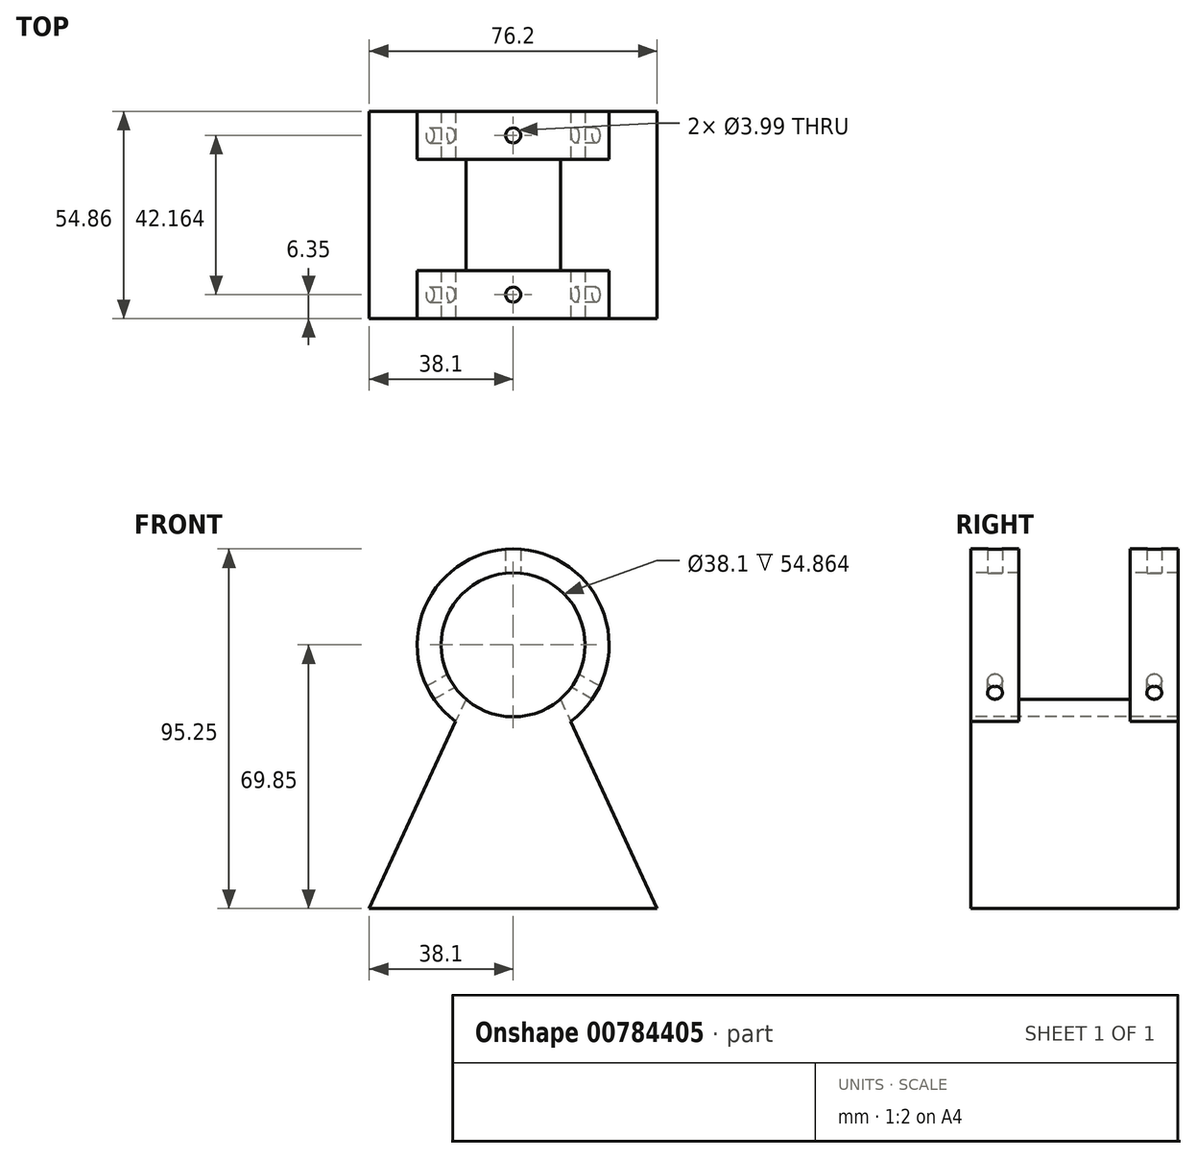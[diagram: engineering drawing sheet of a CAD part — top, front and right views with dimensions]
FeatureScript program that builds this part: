
annotation { "Feature Type Name" : "Feature", "Feature Type Description" : "" }
export const myFeature = defineFeature(function(context is Context, id is Id, definition is map)
    precondition{}
    {
        {
            var Q0;
            Q0=qCreatedBy(makeId("Front.planeOp"),FACE);
            var sketch = newSketch(context, id + "F0", { "sketchPlane" : qUnion([Q0])});
            skCircle(sketch, "E0", {"center": v(0, 69.85) * mm, "radius": 19.05 * mm});
            skArc(sketch, "E1", {"start": v(15.24, 49.53) * mm, "mid": v(0, 95.25) * mm, "end": v(-15.24, 49.53) * mm});
            skLineSegment(sketch, "E2", {"start": v(0, 44.45) * mm, "end": v(0, 49.53) * mm, "construction": true});
            skLineSegment(sketch, "E3", {"start": v(0, 49.53) * mm, "end": v(-15.24, 49.53) * mm, "construction": true});
            skLineSegment(sketch, "E4", {"start": v(-15.24, 49.53) * mm, "end": v(-38.1, 0) * mm});
            skLineSegment(sketch, "E5", {"start": v(-38.1, 0) * mm, "end": v(38.1, 0) * mm});
            skLineSegment(sketch, "E6", {"start": v(38.1, 0) * mm, "end": v(15.24, 49.53) * mm});
            skSolve(sketch);
        }
        {
            var Q0;
            Q0 = qSketchRegion(id + "F0", true);
            extrude(context, id + "F1", {"entities" : qUnion([Q0]), "oppositeDirection" : true, "depth" : 54.86 * mm, "offsetDistance" : 25.4 * mm});
        }
        {
            var Q0;
            Q0=qCreatedBy(makeId("Top.planeOp"),FACE);
            cPlane(context, id + "F2", {"entities" : qUnion([Q0]), "cplaneType" : CPlaneType.OFFSET, "offset" : 12.7 * mm, "width" : 152.4 * mm, "height" : 152.4 * mm});
        }
        {
            var Q0;
            Q0=qCreatedBy(id+"F2.planeOp",FACE);
            var sketch = newSketch(context, id + "F3", { "sketchPlane" : qUnion([Q0])});
            skLineSegment(sketch, "E7.bottom", {"start": v(-38.1, 12.7) * mm, "end": v(38.1, 12.7) * mm});
            skLineSegment(sketch, "E7.top", {"start": v(-38.1, 42.16) * mm, "end": v(38.1, 42.16) * mm});
            skLineSegment(sketch, "E7.left", {"start": v(-38.1, 12.7) * mm, "end": v(-38.1, 42.16) * mm});
            skLineSegment(sketch, "E7.right", {"start": v(38.1, 12.7) * mm, "end": v(38.1, 42.16) * mm});
            skLineSegment(sketch, "E8", {"start": v(0, 12.7) * mm, "end": v(0, 0) * mm, "construction": true});
            skLineSegment(sketch, "E9", {"start": v(0, 42.16) * mm, "end": v(0, 54.86) * mm, "construction": true});
            skSolve(sketch);
        }
        {
            var Q0;
            Q0 = qSketchRegion(id + "F3", true);
            extrude(context, id + "F4", {"entities" : qUnion([Q0]), "operationType" : NewBodyOperationType.REMOVE, "endBound" : BoundingType.THROUGH_ALL, "depth" : 25.4 * mm, "offsetDistance" : 25.4 * mm});
        }
        {
            var Q0;
            Q0=qCreatedBy(makeId("Right.planeOp"),FACE);
            var sketch = newSketch(context, id + "F5", { "sketchPlane" : qUnion([Q0])});
            skLineSegment(sketch, "E10", {"start": v(-9, 69.85) * mm, "end": v(66.82, 69.85) * mm, "construction": true});
            skSolve(sketch);
        }
        {
            var Q0;
            Q0=sQuery(id+"F5.wireOp",EDGE,"E10");
            cPlane(context, id + "F6", {"entities" : qUnion([Q0]), "cplaneType" : CPlaneType.LINE_ANGLE, "offset" : 25.4 * mm, "angle" : 0 * degree, "width" : 152.4 * mm, "height" : 152.4 * mm});
        }
        {
            var Q0;
            Q0=sQuery(id+"F5.wireOp",EDGE,"E10");
            cPlane(context, id + "F7", {"entities" : qUnion([Q0]), "cplaneType" : CPlaneType.LINE_ANGLE, "offset" : 25.4 * mm, "angle" : 60 * degree, "width" : 152.4 * mm, "height" : 152.4 * mm});
        }
        {
            var Q0;
            Q0=sQuery(id+"F5.wireOp",EDGE,"E10");
            cPlane(context, id + "F8", {"entities" : qUnion([Q0]), "cplaneType" : CPlaneType.LINE_ANGLE, "offset" : 25.4 * mm, "angle" : 60 * degree, "oppositeDirection" : true, "width" : 152.4 * mm, "height" : 152.4 * mm});
        }
        {
            var Q0;
            Q0=qCreatedBy(id+"F6.planeOp",FACE);
            var sketch = newSketch(context, id + "F9", { "sketchPlane" : qUnion([Q0])});
            skCircle(sketch, "E11", {"center": v(0, 6.35) * mm, "radius": 2 * mm});
            skCircle(sketch, "E12", {"center": v(0, 48.51) * mm, "radius": 2 * mm});
            skLineSegment(sketch, "E13", {"start": v(0, 48.51) * mm, "end": v(0, 54.86) * mm, "construction": true});
            skLineSegment(sketch, "E14", {"start": v(0, 6.35) * mm, "end": v(0, 0) * mm, "construction": true});
            skLineSegment(sketch, "E15", {"start": v(0, 6.35) * mm, "end": v(0, 12.7) * mm, "construction": true});
            skSolve(sketch);
        }
        {
            var Q0;
            Q0 = qSketchRegion(id + "F9", true);
            extrude(context, id + "F10", {"entities" : qUnion([Q0]), "operationType" : NewBodyOperationType.REMOVE, "endBound" : BoundingType.THROUGH_ALL, "depth" : 25.4 * mm, "offsetDistance" : 25.4 * mm});
        }
        {
            var Q0;
            Q0=qCreatedBy(id+"F7.planeOp",FACE);
            var sketch = newSketch(context, id + "F11", { "sketchPlane" : qUnion([Q0])});
            skCircle(sketch, "E16", {"center": v(6.35, 60.5) * mm, "radius": 2 * mm});
            skCircle(sketch, "E17", {"center": v(48.51, 60.5) * mm, "radius": 2 * mm});
            skLineSegment(sketch, "E18", {"start": v(6.35, 60.5) * mm, "end": v(0, 60.5) * mm, "construction": true});
            skLineSegment(sketch, "E19", {"start": v(6.35, 60.5) * mm, "end": v(12.7, 60.5) * mm, "construction": true});
            skLineSegment(sketch, "E20", {"start": v(48.51, 60.5) * mm, "end": v(42.16, 60.5) * mm, "construction": true});
            skSolve(sketch);
        }
        {
            var Q0;
            Q0 = qSketchRegion(id + "F11", true);
            extrude(context, id + "F12", {"entities" : qUnion([Q0]), "operationType" : NewBodyOperationType.REMOVE, "endBound" : BoundingType.THROUGH_ALL, "oppositeDirection" : true, "depth" : 25.4 * mm, "offsetDistance" : 25.4 * mm});
        }
        {
            var Q0;
            Q0=qCreatedBy(id+"F8.planeOp",FACE);
            var sketch = newSketch(context, id + "F13", { "sketchPlane" : qUnion([Q0])});
            skCircle(sketch, "E21", {"center": v(-48.51, 60.5) * mm, "radius": 2 * mm});
            skCircle(sketch, "E22", {"center": v(-6.35, 60.5) * mm, "radius": 2 * mm});
            skLineSegment(sketch, "E23", {"start": v(0, 60.5) * mm, "end": v(-6.35, 60.5) * mm, "construction": true});
            skLineSegment(sketch, "E24", {"start": v(-48.51, 60.5) * mm, "end": v(-42.16, 60.5) * mm, "construction": true});
            skLineSegment(sketch, "E25", {"start": v(-6.35, 60.5) * mm, "end": v(-12.7, 60.5) * mm, "construction": true});
            skSolve(sketch);
        }
        {
            var Q0;
            Q0 = qSketchRegion(id + "F13", true);
            extrude(context, id + "F14", {"entities" : qUnion([Q0]), "operationType" : NewBodyOperationType.REMOVE, "endBound" : BoundingType.THROUGH_ALL, "oppositeDirection" : true, "depth" : 25.4 * mm, "offsetDistance" : 25.4 * mm});
        }
        {
            var Q0;
            Q0=makeQuery(id+"F1.opExtrude","CAP_FACE",FACE,{"disambiguationData":[OSD([sQuery(id+"F0.wireOp",EDGE,"E0"),sQuery(id+"F0.wireOp",EDGE,"E1"),sQuery(id+"F0.wireOp",EDGE,"E4"),sQuery(id+"F0.wireOp",EDGE,"E5"),sQuery(id+"F0.wireOp",EDGE,"E6")])],"isStart":true});
            var sketch = newSketch(context, id + "F15", { "sketchPlane" : qUnion([Q0])});
            skLineSegment(sketch, "E26.0", {"start": v(-9.7, 46.38) * mm, "end": v(-28.18, 6.35) * mm});
            skLineSegment(sketch, "E27.0", {"start": v(28.18, 6.35) * mm, "end": v(9.7, 46.38) * mm});
            skLineSegment(sketch, "E28.0", {"start": v(-28.18, 6.35) * mm, "end": v(28.18, 6.35) * mm});
            skArc(sketch, "E29.0", {"start": v(-9.7, 46.38) * mm, "mid": v(0, 44.45) * mm, "end": v(9.7, 46.38) * mm});
            skSolve(sketch);
        }
        {
            var Q0;
            Q0=makeQuery(id+"F1.opExtrude","CAP_FACE",FACE,{"disambiguationData":[OSD([sQuery(id+"F0.wireOp",EDGE,"E0"),sQuery(id+"F0.wireOp",EDGE,"E1"),sQuery(id+"F0.wireOp",EDGE,"E4"),sQuery(id+"F0.wireOp",EDGE,"E5"),sQuery(id+"F0.wireOp",EDGE,"E6")])],"isStart":true});
            var sketch = newSketch(context, id + "F16", { "sketchPlane" : qUnion([Q0])});
            skLineSegment(sketch, "E30", {"start": v(-15.24, 49.53) * mm, "end": v(-12.5, 55.47) * mm});
            skLineSegment(sketch, "E31", {"start": v(15.24, 49.53) * mm, "end": v(12.5, 55.47) * mm});
            skArc(sketch, "E32", {"start": v(-12.5, 55.47) * mm, "mid": v(0, 50.8) * mm, "end": v(12.5, 55.47) * mm});
            skLineSegment(sketch, "E33", {"start": v(-12.5, 55.47) * mm, "end": v(-38.1, 0) * mm});
            skLineSegment(sketch, "E34", {"start": v(-38.1, 0) * mm, "end": v(38.1, 0) * mm});
            skLineSegment(sketch, "E35", {"start": v(38.1, 0) * mm, "end": v(12.5, 55.47) * mm});
            skSolve(sketch);
        }
        {
            var Q0;
            Q0 = qSketchRegion(id + "F16", true);
            var Q1;
            Q1=makeQuery(id+"F4.boolean.opBoolean","COPY",FACE,{"derivedFrom":makeQuery(id+"F4.opExtrude","SWEPT_FACE",FACE,{"disambiguationData":[OSD([sQuery(id+"F3.wireOp",EDGE,"E7.top")])]})});
            extrude(context, id + "F17", {"entities" : qUnion([Q0]), "operationType" : NewBodyOperationType.ADD, "endBound" : BoundingType.UP_TO_SURFACE, "oppositeDirection" : true, "depth" : 25.4 * mm, "endBoundEntityFace" : qUnion([Q1]), "offsetDistance" : 25.4 * mm});
        }
    });
